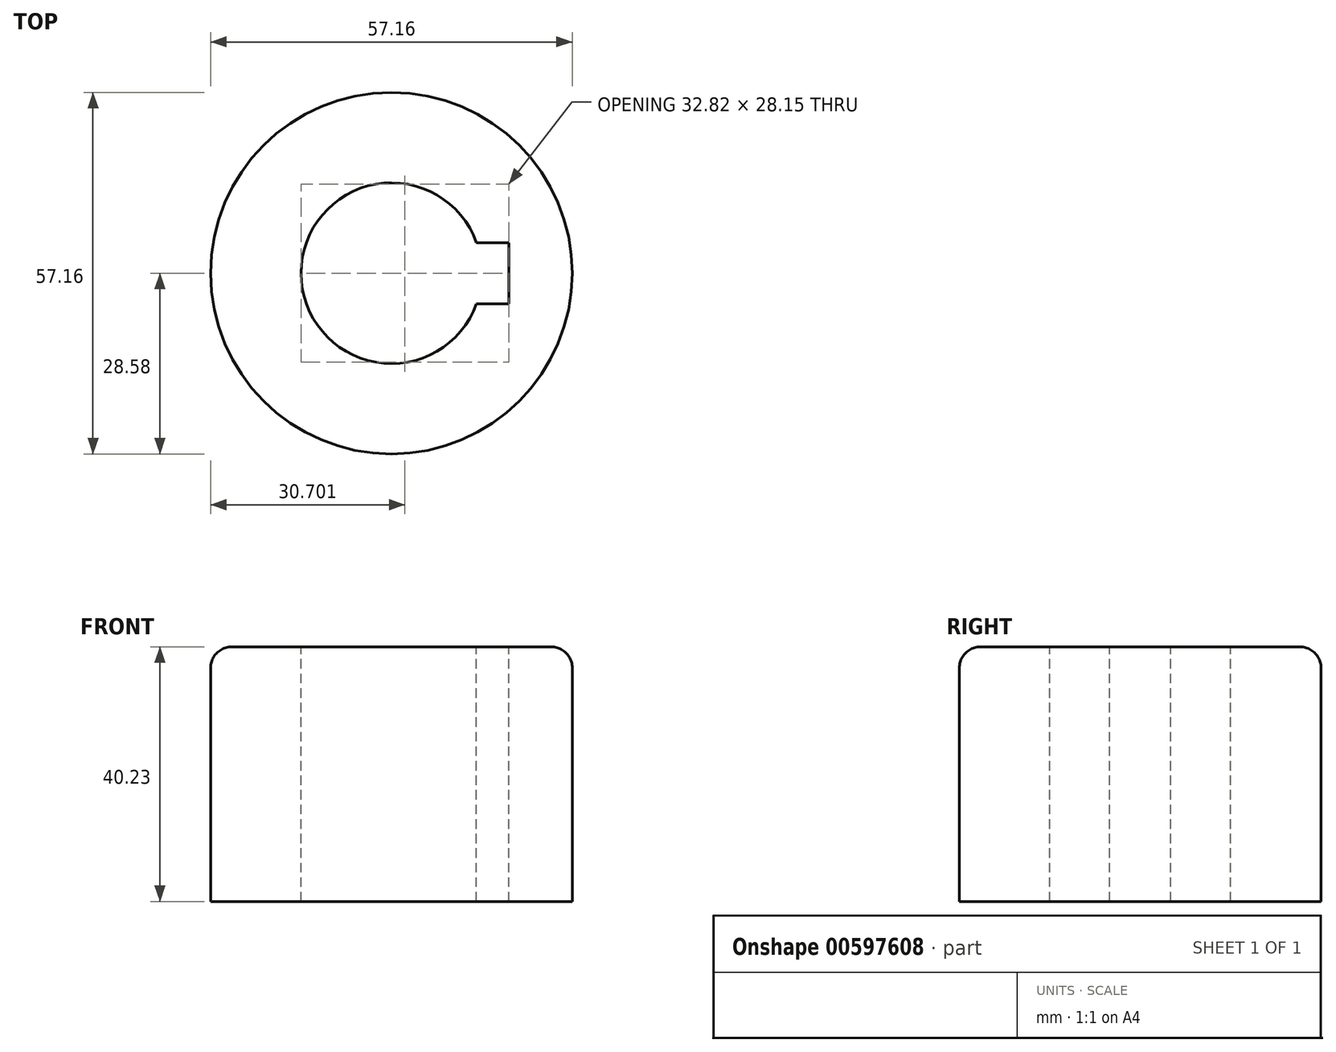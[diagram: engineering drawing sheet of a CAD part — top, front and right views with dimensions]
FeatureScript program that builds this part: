
annotation { "Feature Type Name" : "Feature", "Feature Type Description" : "" }
export const myFeature = defineFeature(function(context is Context, id is Id, definition is map)
    precondition{}
    {
        {
            var Q0;
            Q0=qCreatedBy(makeId("Top.planeOp"),FACE);
            var sketch = newSketch(context, id + "F0", { "sketchPlane" : qUnion([Q0])});
            skCircle(sketch, "E0", {"center": v(0, 0) * mm, "radius": 28.58 * mm});
            skSolve(sketch);
        }
        {
            var Q0;
            Q0 = qSketchRegion(id + "F0", true);
            extrude(context, id + "F1", {"entities" : qUnion([Q0]), "depth" : 40.23 * mm, "offsetDistance" : 25.4 * mm});
        }
        {
            var Q0;
            Q0=makeQuery(id+"F1.opExtrude","CAP_EDGE",EDGE,{"disambiguationData":[OSD([sQuery(id+"F0.wireOp",EDGE,"E0")])],"isStart":false});
            fillet(context, id + "F2", {"entities" : qUnion([Q0]), "radius" : 3.3 * mm, "tangentPropagation" : true, "allowEdgeOverflow" : false});
        }
        {
            var Q0;
            Q0=makeQuery(id+"F1.opExtrude","CAP_FACE",FACE,{"disambiguationData":[OSD([sQuery(id+"F0.wireOp",EDGE,"E0")])],"isStart":false});
            var sketch = newSketch(context, id + "F3", { "sketchPlane" : qUnion([Q0])});
            skArc(sketch, "E1", {"start": v(13.45, 4.83) * mm, "mid": v(-14.29, 0) * mm, "end": v(13.45, -4.83) * mm});
            skLineSegment(sketch, "E2", {"start": v(13.45, 4.83) * mm, "end": v(18.53, 4.83) * mm});
            skLineSegment(sketch, "E3", {"start": v(18.53, 4.83) * mm, "end": v(18.53, -4.83) * mm});
            skLineSegment(sketch, "E4", {"start": v(18.53, -4.83) * mm, "end": v(13.45, -4.83) * mm});
            skSolve(sketch);
        }
        {
            var Q0;
            Q0 = qSketchRegion(id + "F3", true);
            extrude(context, id + "F4", {"entities" : qUnion([Q0]), "operationType" : NewBodyOperationType.REMOVE, "endBound" : BoundingType.UP_TO_NEXT, "oppositeDirection" : true, "depth" : 25.4 * mm, "offsetDistance" : 25.4 * mm});
        }
    });
